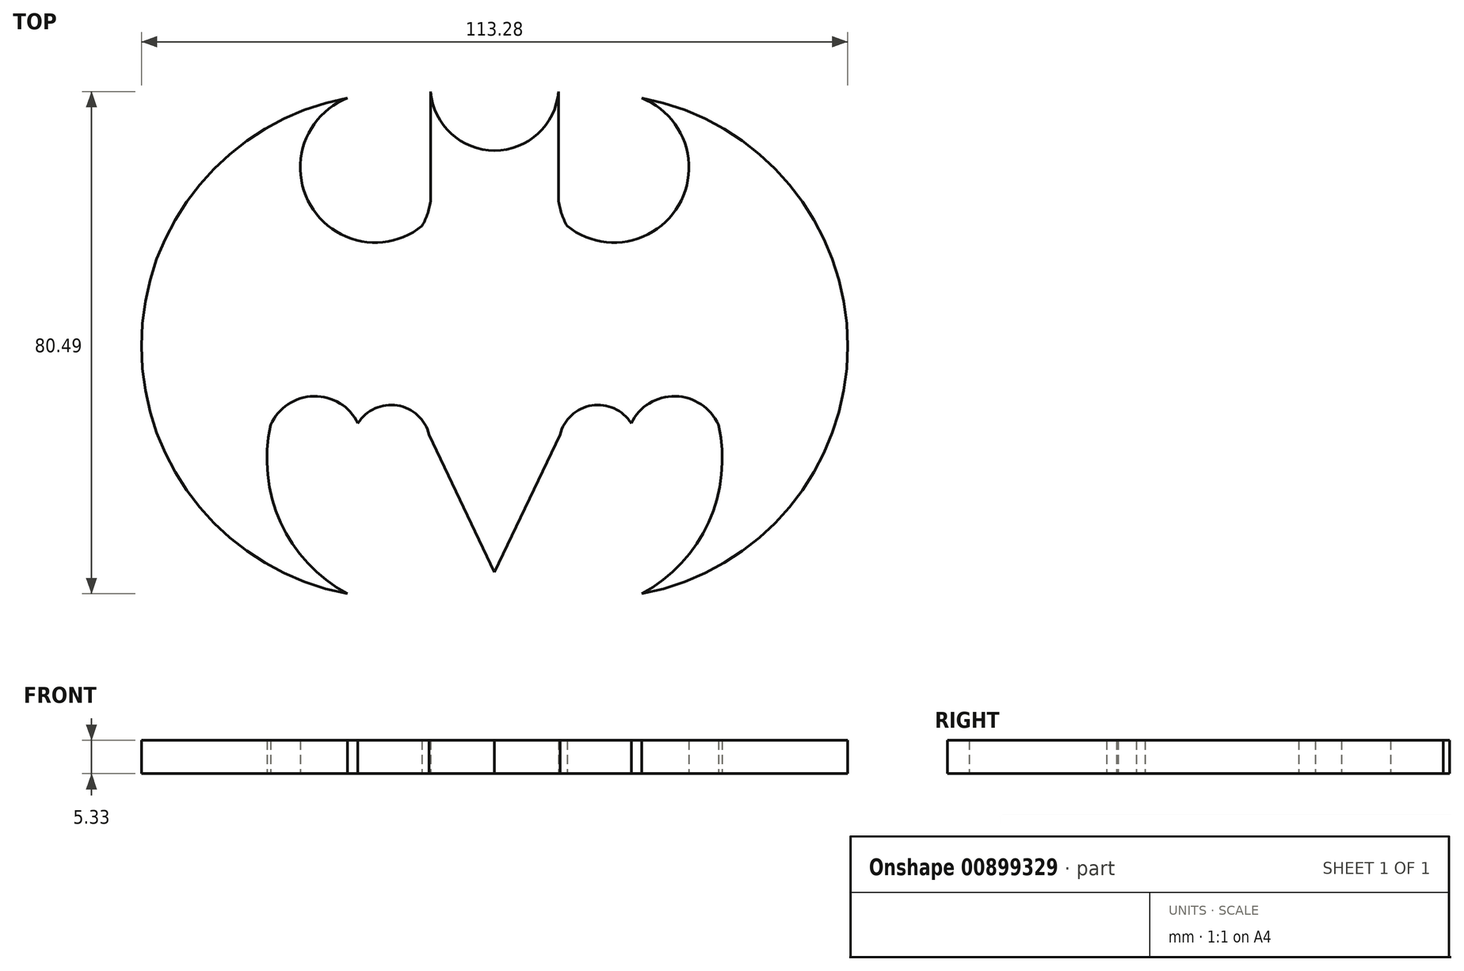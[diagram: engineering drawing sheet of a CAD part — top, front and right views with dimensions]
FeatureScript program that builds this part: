
annotation { "Feature Type Name" : "Feature", "Feature Type Description" : "" }
export const myFeature = defineFeature(function(context is Context, id is Id, definition is map)
    precondition{}
    {
        {
            var Q0;
            Q0=qCreatedBy(makeId("Top.planeOp"),FACE);
            var sketch = newSketch(context, id + "F0", { "sketchPlane" : qUnion([Q0])});
            skPoint(sketch, "E0.third.point", {"position": v(-25.5, -22.49) * mm});
            skPoint(sketch, "E1.second.point", {"position": v(-9.94, -32) * mm});
            skPoint(sketch, "E1.third.point", {"position": v(-15.7, -36.81) * mm});
            skPoint(sketch, "E2", {"position": v(0, 16.73) * mm});
            skPoint(sketch, "E3.orphan", {"position": v(-15.86, -1.54) * mm});
            skPoint(sketch, "E4.orphan", {"position": v(0, -28.3) * mm});
            skPoint(sketch, "E5.orphan", {"position": v(-7.02, -54.26) * mm});
            skPoint(sketch, "E6.end.orphan", {"position": v(-15.86, -54.26) * mm});
            skArc(sketch, "E7", {"start": v(-21.9, -28.75) * mm, "mid": v(-32.22, -25.22) * mm, "end": v(-35.78, -35.52) * mm});
            skLineSegment(sketch, "E8", {"start": v(0, 0) * mm, "end": v(0, 55.04) * mm});
            skArc(sketch, "E9.MirrorCS", {"start": v(21.9, -28.75) * mm, "mid": v(32.22, -25.22) * mm, "end": v(35.78, -35.52) * mm});
            skArc(sketch, "E10", {"start": v(10.25, 7.08) * mm, "mid": v(10.71, 4.88) * mm, "end": v(11.63, 2.84) * mm});
            skLineSegment(sketch, "E11", {"start": v(10.25, 7.08) * mm, "end": v(10.25, 24.4) * mm});
            skLineSegment(sketch, "E12.MirrorCS", {"start": v(-10.25, 7.08) * mm, "end": v(-10.25, 24.4) * mm});
            skArc(sketch, "E13.MirrorCS", {"start": v(-10.25, 7.08) * mm, "mid": v(-10.71, 4.88) * mm, "end": v(-11.63, 2.84) * mm});
            skArc(sketch, "E14", {"start": v(-10.25, 24.4) * mm, "mid": v(0, 14.94) * mm, "end": v(10.25, 24.4) * mm});
            skArc(sketch, "E15", {"start": v(21.9, -28.75) * mm, "mid": v(14.3, -26.27) * mm, "end": v(10.4, -33.26) * mm});
            skLineSegment(sketch, "E16", {"start": v(10.48, -30.6) * mm, "end": v(0, -52.63) * mm});
            skArc(sketch, "E17.MirrorCS", {"start": v(-21.9, -28.75) * mm, "mid": v(-14.3, -26.27) * mm, "end": v(-10.4, -33.26) * mm});
            skLineSegment(sketch, "E18.MirrorCS", {"start": v(-10.48, -30.6) * mm, "end": v(0, -52.63) * mm});
            skArc(sketch, "E19", {"start": v(-23.58, 23.36) * mm, "mid": v(-56.64, -16.37) * mm, "end": v(-23.58, -56.1) * mm});
            skArc(sketch, "E20", {"start": v(-23.58, 23.36) * mm, "mid": v(-29.52, 6.16) * mm, "end": v(-11.63, 2.84) * mm});
            skArc(sketch, "E21", {"start": v(-35.88, -29.01) * mm, "mid": v(-34.32, -44.64) * mm, "end": v(-23.58, -56.1) * mm});
            skArc(sketch, "E22.MirrorCS", {"start": v(23.58, 23.36) * mm, "mid": v(29.52, 6.16) * mm, "end": v(11.63, 2.84) * mm});
            skArc(sketch, "E23.MirrorCS", {"start": v(23.58, 23.36) * mm, "mid": v(56.64, -16.37) * mm, "end": v(23.58, -56.1) * mm});
            skArc(sketch, "E24.MirrorCS", {"start": v(35.88, -29.01) * mm, "mid": v(34.32, -44.64) * mm, "end": v(23.58, -56.1) * mm});
            skSolve(sketch);
        }
        {
            var Q0;
            Q0=qSketchRegion(id+"F0",true);
            extrude(context, id + "F1", {"entities" : qUnion([Q0]), "depth" : 5.33 * mm});
        }
    });
